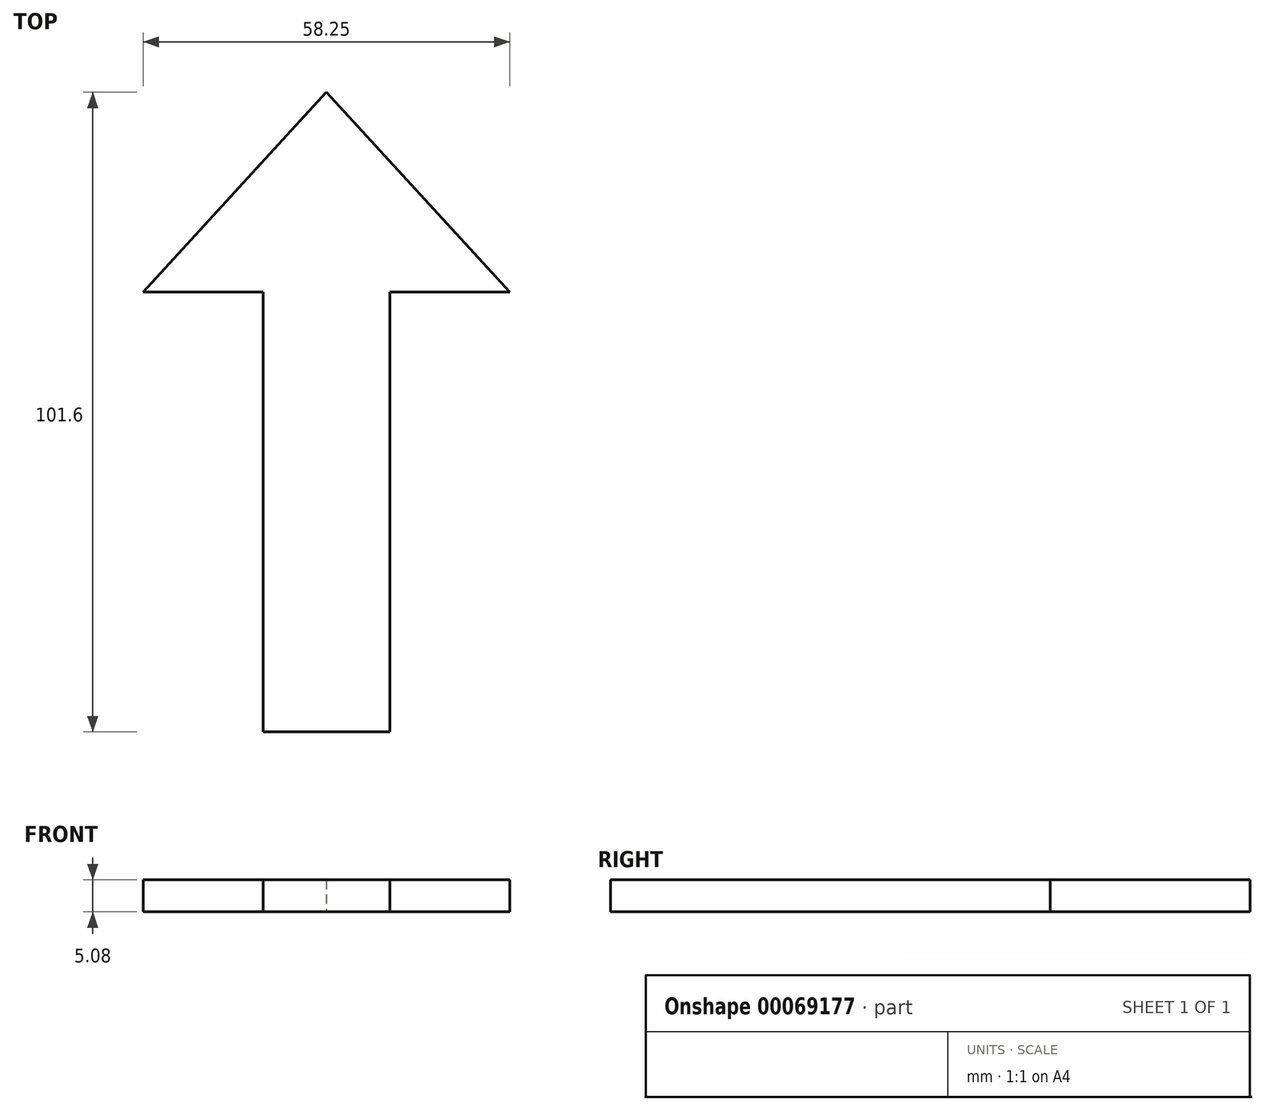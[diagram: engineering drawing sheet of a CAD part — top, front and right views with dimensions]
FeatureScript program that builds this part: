
annotation { "Feature Type Name" : "Feature", "Feature Type Description" : "" }
export const myFeature = defineFeature(function(context is Context, id is Id, definition is map)
    precondition{}
    {
        {
            var Q0;
            Q0=qCreatedBy(makeId("Top.planeOp"),FACE);
            var sketch = newSketch(context, id + "F0", { "sketchPlane" : qUnion([Q0])});
            skLineSegment(sketch, "E0.bottom", {"start": v(0, 0) * mm, "end": v(20.15, 0) * mm});
            skLineSegment(sketch, "E0.top", {"start": v(0, 69.85) * mm, "end": v(20.15, 69.85) * mm});
            skLineSegment(sketch, "E0.left", {"start": v(0, 0) * mm, "end": v(0, 69.85) * mm});
            skLineSegment(sketch, "E0.right", {"start": v(20.15, 0) * mm, "end": v(20.15, 69.85) * mm});
            skLineSegment(sketch, "E1", {"start": v(0, 69.85) * mm, "end": v(-19.05, 69.85) * mm});
            skPoint(sketch, "E2", {"position": v(10.07, 69.85) * mm});
            skLineSegment(sketch, "E3", {"start": v(-19.05, 69.85) * mm, "end": v(10.07, 101.6) * mm});
            skLineSegment(sketch, "E4", {"start": v(10.07, 101.6) * mm, "end": v(10.07, 69.85) * mm, "construction": true});
            skLineSegment(sketch, "E5.MirrorCS", {"start": v(39.2, 69.85) * mm, "end": v(10.07, 101.6) * mm});
            skLineSegment(sketch, "E6.MirrorCS", {"start": v(20.15, 69.85) * mm, "end": v(39.2, 69.85) * mm});
            skSolve(sketch);
        }
        {
            var Q0;
            Q0 = qSketchRegion(id + "F0", true);
            extrude(context, id + "F1", {"entities" : qUnion([Q0]), "depth" : 5.08 * mm});
        }
    });
